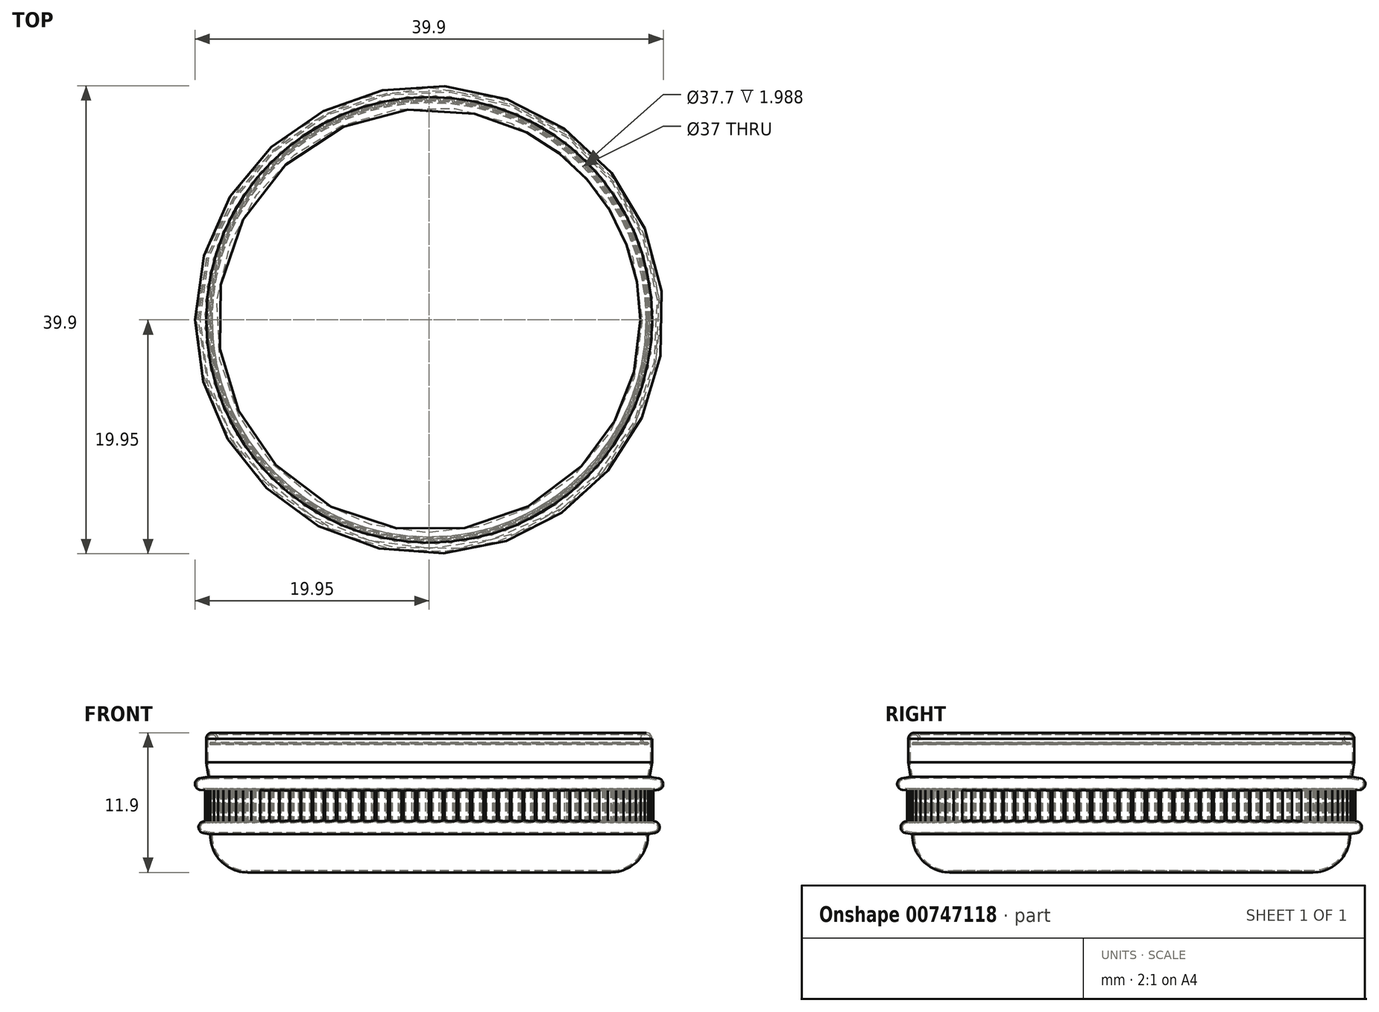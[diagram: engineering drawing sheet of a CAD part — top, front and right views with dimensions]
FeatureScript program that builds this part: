
annotation { "Feature Type Name" : "Feature", "Feature Type Description" : "" }
export const myFeature = defineFeature(function(context is Context, id is Id, definition is map)
    precondition{}
    {
        {
            var Q0;
            Q0=qCreatedBy(makeId("Top.planeOp"),FACE);
            var sketch = newSketch(context, id + "F0", { "sketchPlane" : qUnion([Q0])});
            skCircle(sketch, "E0", {"center": v(0, 0) * mm, "radius": 18.65 * mm});
            skSolve(sketch);
        }
        {
            var Q0;
            Q0 = qSketchRegion(id + "F0", true);
            extrude(context, id + "F1", {"entities" : qUnion([Q0]), "depth" : 11.4 * mm, "offsetDistance" : 25 * mm});
        }
        {
            var Q0;
            Q0=makeQuery(id+"F1.opExtrude","CAP_EDGE",EDGE,{"disambiguationData":[OSD([sQuery(id+"F0.wireOp",EDGE,"E0")])],"isStart":true});
            fillet(context, id + "F2", {"entities" : qUnion([Q0]), "radius" : 3.17 * mm, "tangentPropagation" : true, "allowEdgeOverflow" : false});
        }
        {
            var Q0;
            Q0=makeQuery(id+"F1.opExtrude","CAP_FACE",FACE,{"disambiguationData":[OSD([sQuery(id+"F0.wireOp",EDGE,"E0")])],"isStart":false});
            cPlane(context, id + "F3", {"entities" : qUnion([Q0]), "cplaneType" : CPlaneType.OFFSET, "offset" : 3.25 * mm, "oppositeDirection" : true, "width" : 150 * mm, "height" : 150 * mm});
        }
        {
            var Q0;
            Q0=makeQuery(id+"F1.opExtrude","CAP_FACE",FACE,{"disambiguationData":[OSD([sQuery(id+"F0.wireOp",EDGE,"E0")])],"isStart":false});
            cPlane(context, id + "F4", {"entities" : qUnion([Q0]), "cplaneType" : CPlaneType.OFFSET, "offset" : 8.15 * mm, "oppositeDirection" : true, "width" : 150 * mm, "height" : 150 * mm});
        }
        {
            var Q0;
            Q0=qCreatedBy(makeId("Front.planeOp"),FACE);
            var sketch = newSketch(context, id + "F5", { "sketchPlane" : qUnion([Q0])});
            skLineSegment(sketch, "E1", {"start": v(-18.65, 3.18) * mm, "end": v(-18.65, 8.15) * mm});
            skLineSegment(sketch, "E2", {"start": v(-18.65, 11.4) * mm, "end": v(-18.65, 3.18) * mm});
            skLineSegment(sketch, "E3", {"start": v(-18.65, 6.95) * mm, "end": v(-19.5, 7.03) * mm});
            skLineSegment(sketch, "E4", {"start": v(-18.65, 3.25) * mm, "end": v(-19.24, 3.36) * mm});
            skLineSegment(sketch, "E5", {"start": v(-18.65, 4.45) * mm, "end": v(-19.24, 4.34) * mm});
            skArc(sketch, "E6", {"start": v(-19.53, 8.02) * mm, "mid": v(-19.95, 7.51) * mm, "end": v(-19.5, 7.03) * mm});
            skArc(sketch, "E7", {"start": v(-19.24, 4.34) * mm, "mid": v(-19.65, 3.85) * mm, "end": v(-19.24, 3.36) * mm});
            skLineSegment(sketch, "E8", {"start": v(-19, 11.4) * mm, "end": v(-18.65, 11.4) * mm});
            skLineSegment(sketch, "E9", {"start": v(-19.53, 8.02) * mm, "end": v(-18.8, 8.15) * mm});
            skLineSegment(sketch, "E10", {"start": v(-18.8, 8.15) * mm, "end": v(-19, 9.4) * mm});
            skLineSegment(sketch, "E11", {"start": v(-19, 9.4) * mm, "end": v(-19, 11.4) * mm});
            skSolve(sketch);
        }
        {
            var Q0;
            Q0 = qSketchRegion(id + "F5", true);
            var Q1;
            Q1=makeQuery(id+"F1.opExtrude","CAP_EDGE",EDGE,{"disambiguationData":[OSD([sQuery(id+"F0.wireOp",EDGE,"E0")])],"isStart":false});
            revolve(context, id + "F6", {"operationType" : NewBodyOperationType.ADD, "surfaceOperationType" : NewSurfaceOperationType.NEW, "entities" : qUnion([Q0]), "axis" : qUnion([Q1]), "revolveType" : RevolveType.FULL});
        }
        {
            var Q0;
            Q0=qCreatedBy(id+"F3.planeOp",FACE);
            cPlane(context, id + "F7", {"entities" : qUnion([Q0]), "cplaneType" : CPlaneType.OFFSET, "offset" : 2.45 * mm, "oppositeDirection" : true, "width" : 150 * mm, "height" : 150 * mm});
        }
        {
            var Q0;
            Q0=qCreatedBy(id+"F7.planeOp",FACE);
            var sketch = newSketch(context, id + "F8", { "sketchPlane" : qUnion([Q0])});
            skArc(sketch, "E12", {"start": v(1, 18.57) * mm, "mid": v(0.51, 19.1) * mm, "end": v(0, 18.6) * mm});
            skArc(sketch, "E13", {"start": v(1, 18.57) * mm, "mid": v(0.5, 18.6) * mm, "end": v(0, 18.6) * mm});
            skArc(sketch, "E14.1.0", {"start": v(-0.17, 18.6) * mm, "mid": v(-0.67, 18.59) * mm, "end": v(-1.17, 18.56) * mm});
            skArc(sketch, "E14.1.1", {"start": v(-0.17, 18.6) * mm, "mid": v(-0.69, 19.09) * mm, "end": v(-1.17, 18.56) * mm});
            skArc(sketch, "E14.2.0", {"start": v(-1.34, 18.55) * mm, "mid": v(-1.83, 18.5) * mm, "end": v(-2.33, 18.45) * mm});
            skArc(sketch, "E14.2.1", {"start": v(-1.34, 18.55) * mm, "mid": v(-1.88, 19) * mm, "end": v(-2.33, 18.45) * mm});
            skArc(sketch, "E14.3.0", {"start": v(-2.5, 18.43) * mm, "mid": v(-3, 18.36) * mm, "end": v(-3.49, 18.27) * mm});
            skArc(sketch, "E14.3.1", {"start": v(-2.5, 18.43) * mm, "mid": v(-3.07, 18.85) * mm, "end": v(-3.49, 18.27) * mm});
            skArc(sketch, "E14.4.0", {"start": v(-3.65, 18.24) * mm, "mid": v(-4.14, 18.13) * mm, "end": v(-4.63, 18.02) * mm});
            skArc(sketch, "E14.4.1", {"start": v(-3.65, 18.24) * mm, "mid": v(-4.25, 18.62) * mm, "end": v(-4.63, 18.02) * mm});
            skArc(sketch, "E14.5.0", {"start": v(-4.79, 17.97) * mm, "mid": v(-5.27, 17.84) * mm, "end": v(-5.75, 17.69) * mm});
            skArc(sketch, "E14.5.1", {"start": v(-4.79, 17.97) * mm, "mid": v(-5.41, 18.32) * mm, "end": v(-5.75, 17.69) * mm});
            skArc(sketch, "E14.6.0", {"start": v(-5.9, 17.64) * mm, "mid": v(-6.38, 17.47) * mm, "end": v(-6.85, 17.3) * mm});
            skArc(sketch, "E14.6.1", {"start": v(-5.9, 17.64) * mm, "mid": v(-6.55, 17.94) * mm, "end": v(-6.85, 17.3) * mm});
            skArc(sketch, "E14.7.0", {"start": v(-7, 17.23) * mm, "mid": v(-7.46, 17.04) * mm, "end": v(-7.92, 16.83) * mm});
            skArc(sketch, "E14.7.1", {"start": v(-7, 17.23) * mm, "mid": v(-7.66, 17.5) * mm, "end": v(-7.92, 16.83) * mm});
            skArc(sketch, "E14.8.0", {"start": v(-8.07, 16.76) * mm, "mid": v(-8.52, 16.53) * mm, "end": v(-8.96, 16.3) * mm});
            skArc(sketch, "E14.8.1", {"start": v(-8.07, 16.76) * mm, "mid": v(-8.75, 16.98) * mm, "end": v(-8.96, 16.3) * mm});
            skArc(sketch, "E14.9.0", {"start": v(-9.1, 16.22) * mm, "mid": v(-9.54, 15.97) * mm, "end": v(-9.97, 15.7) * mm});
            skArc(sketch, "E14.9.1", {"start": v(-9.1, 16.22) * mm, "mid": v(-9.8, 16.4) * mm, "end": v(-9.97, 15.7) * mm});
            skArc(sketch, "E14.10.0", {"start": v(-10.1, 15.61) * mm, "mid": v(-10.52, 15.34) * mm, "end": v(-10.93, 15.05) * mm});
            skArc(sketch, "E14.10.1", {"start": v(-10.1, 15.61) * mm, "mid": v(-10.8, 15.75) * mm, "end": v(-10.93, 15.05) * mm});
            skArc(sketch, "E14.11.0", {"start": v(-11.07, 14.95) * mm, "mid": v(-11.47, 14.65) * mm, "end": v(-11.86, 14.33) * mm});
            skArc(sketch, "E14.11.1", {"start": v(-11.07, 14.95) * mm, "mid": v(-11.77, 15.04) * mm, "end": v(-11.86, 14.33) * mm});
            skArc(sketch, "E14.12.0", {"start": v(-11.99, 14.22) * mm, "mid": v(-12.36, 13.9) * mm, "end": v(-12.73, 13.56) * mm});
            skArc(sketch, "E14.12.1", {"start": v(-11.99, 14.22) * mm, "mid": v(-12.7, 14.27) * mm, "end": v(-12.73, 13.56) * mm});
            skArc(sketch, "E14.13.0", {"start": v(-12.85, 13.44) * mm, "mid": v(-13.21, 13.1) * mm, "end": v(-13.56, 12.73) * mm});
            skArc(sketch, "E14.13.1", {"start": v(-12.85, 13.44) * mm, "mid": v(-13.57, 13.44) * mm, "end": v(-13.56, 12.73) * mm});
            skArc(sketch, "E14.14.0", {"start": v(-13.67, 12.6) * mm, "mid": v(-14, 12.24) * mm, "end": v(-14.33, 11.86) * mm});
            skArc(sketch, "E14.14.1", {"start": v(-13.67, 12.6) * mm, "mid": v(-14.38, 12.57) * mm, "end": v(-14.33, 11.86) * mm});
            skArc(sketch, "E14.15.0", {"start": v(-14.44, 11.73) * mm, "mid": v(-14.75, 11.33) * mm, "end": v(-15.05, 10.93) * mm});
            skArc(sketch, "E14.15.1", {"start": v(-14.44, 11.73) * mm, "mid": v(-15.14, 11.64) * mm, "end": v(-15.05, 10.93) * mm});
            skArc(sketch, "E14.16.0", {"start": v(-15.15, 10.8) * mm, "mid": v(-15.43, 10.38) * mm, "end": v(-15.7, 9.97) * mm});
            skArc(sketch, "E14.16.1", {"start": v(-15.15, 10.8) * mm, "mid": v(-15.85, 10.66) * mm, "end": v(-15.7, 9.97) * mm});
            skArc(sketch, "E14.17.0", {"start": v(-15.8, 9.82) * mm, "mid": v(-16.05, 9.4) * mm, "end": v(-16.3, 8.96) * mm});
            skArc(sketch, "E14.17.1", {"start": v(-15.8, 9.82) * mm, "mid": v(-16.48, 9.65) * mm, "end": v(-16.3, 8.96) * mm});
            skArc(sketch, "E14.18.0", {"start": v(-16.38, 8.81) * mm, "mid": v(-16.61, 8.37) * mm, "end": v(-16.83, 7.92) * mm});
            skArc(sketch, "E14.18.1", {"start": v(-16.38, 8.81) * mm, "mid": v(-17.06, 8.6) * mm, "end": v(-16.83, 7.92) * mm});
            skArc(sketch, "E14.19.0", {"start": v(-16.9, 7.77) * mm, "mid": v(-17.1, 7.3) * mm, "end": v(-17.3, 6.85) * mm});
            skArc(sketch, "E14.19.1", {"start": v(-16.9, 7.77) * mm, "mid": v(-17.56, 7.5) * mm, "end": v(-17.3, 6.85) * mm});
            skArc(sketch, "E14.20.0", {"start": v(-17.36, 6.7) * mm, "mid": v(-17.53, 6.22) * mm, "end": v(-17.69, 5.75) * mm});
            skArc(sketch, "E14.20.1", {"start": v(-17.36, 6.7) * mm, "mid": v(-18, 6.39) * mm, "end": v(-17.69, 5.75) * mm});
            skArc(sketch, "E14.21.0", {"start": v(-17.74, 5.59) * mm, "mid": v(-17.88, 5.1) * mm, "end": v(-18.02, 4.63) * mm});
            skArc(sketch, "E14.21.1", {"start": v(-17.74, 5.59) * mm, "mid": v(-18.37, 5.25) * mm, "end": v(-18.02, 4.63) * mm});
            skArc(sketch, "E14.22.0", {"start": v(-18.06, 4.46) * mm, "mid": v(-18.17, 3.98) * mm, "end": v(-18.27, 3.49) * mm});
            skArc(sketch, "E14.22.1", {"start": v(-18.06, 4.46) * mm, "mid": v(-18.66, 4.08) * mm, "end": v(-18.27, 3.49) * mm});
            skArc(sketch, "E14.23.0", {"start": v(-18.3, 3.32) * mm, "mid": v(-18.38, 2.83) * mm, "end": v(-18.45, 2.33) * mm});
            skArc(sketch, "E14.23.1", {"start": v(-18.3, 3.32) * mm, "mid": v(-18.88, 2.9) * mm, "end": v(-18.45, 2.33) * mm});
            skArc(sketch, "E14.24.0", {"start": v(-18.47, 2.16) * mm, "mid": v(-18.53, 1.67) * mm, "end": v(-18.56, 1.17) * mm});
            skArc(sketch, "E14.24.1", {"start": v(-18.47, 2.16) * mm, "mid": v(-19.02, 1.71) * mm, "end": v(-18.56, 1.17) * mm});
            skArc(sketch, "E14.25.0", {"start": v(-18.57, 1) * mm, "mid": v(-18.6, 0.5) * mm, "end": v(-18.6, 0) * mm});
            skArc(sketch, "E14.25.1", {"start": v(-18.57, 1) * mm, "mid": v(-19.1, 0.51) * mm, "end": v(-18.6, 0) * mm});
            skArc(sketch, "E14.26.0", {"start": v(-18.6, -0.17) * mm, "mid": v(-18.59, -0.67) * mm, "end": v(-18.56, -1.17) * mm});
            skArc(sketch, "E14.26.1", {"start": v(-18.6, -0.17) * mm, "mid": v(-19.09, -0.69) * mm, "end": v(-18.56, -1.17) * mm});
            skArc(sketch, "E14.27.0", {"start": v(-18.55, -1.34) * mm, "mid": v(-18.5, -1.83) * mm, "end": v(-18.45, -2.33) * mm});
            skArc(sketch, "E14.27.1", {"start": v(-18.55, -1.34) * mm, "mid": v(-19, -1.88) * mm, "end": v(-18.45, -2.33) * mm});
            skArc(sketch, "E14.28.0", {"start": v(-18.43, -2.5) * mm, "mid": v(-18.36, -3) * mm, "end": v(-18.27, -3.49) * mm});
            skArc(sketch, "E14.28.1", {"start": v(-18.43, -2.5) * mm, "mid": v(-18.85, -3.07) * mm, "end": v(-18.27, -3.49) * mm});
            skArc(sketch, "E14.29.0", {"start": v(-18.24, -3.65) * mm, "mid": v(-18.13, -4.14) * mm, "end": v(-18.02, -4.63) * mm});
            skArc(sketch, "E14.29.1", {"start": v(-18.24, -3.65) * mm, "mid": v(-18.62, -4.25) * mm, "end": v(-18.02, -4.63) * mm});
            skArc(sketch, "E14.30.0", {"start": v(-17.97, -4.79) * mm, "mid": v(-17.84, -5.27) * mm, "end": v(-17.69, -5.75) * mm});
            skArc(sketch, "E14.30.1", {"start": v(-17.97, -4.79) * mm, "mid": v(-18.32, -5.41) * mm, "end": v(-17.69, -5.75) * mm});
            skArc(sketch, "E14.31.0", {"start": v(-17.64, -5.9) * mm, "mid": v(-17.47, -6.38) * mm, "end": v(-17.3, -6.85) * mm});
            skArc(sketch, "E14.31.1", {"start": v(-17.64, -5.9) * mm, "mid": v(-17.94, -6.55) * mm, "end": v(-17.3, -6.85) * mm});
            skArc(sketch, "E14.32.0", {"start": v(-17.23, -7) * mm, "mid": v(-17.04, -7.46) * mm, "end": v(-16.83, -7.92) * mm});
            skArc(sketch, "E14.32.1", {"start": v(-17.23, -7) * mm, "mid": v(-17.5, -7.66) * mm, "end": v(-16.83, -7.92) * mm});
            skArc(sketch, "E14.33.0", {"start": v(-16.76, -8.07) * mm, "mid": v(-16.53, -8.52) * mm, "end": v(-16.3, -8.96) * mm});
            skArc(sketch, "E14.33.1", {"start": v(-16.76, -8.07) * mm, "mid": v(-16.98, -8.75) * mm, "end": v(-16.3, -8.96) * mm});
            skArc(sketch, "E14.34.0", {"start": v(-16.22, -9.1) * mm, "mid": v(-15.97, -9.54) * mm, "end": v(-15.7, -9.97) * mm});
            skArc(sketch, "E14.34.1", {"start": v(-16.22, -9.1) * mm, "mid": v(-16.4, -9.8) * mm, "end": v(-15.7, -9.97) * mm});
            skArc(sketch, "E14.35.0", {"start": v(-15.61, -10.1) * mm, "mid": v(-15.34, -10.52) * mm, "end": v(-15.05, -10.93) * mm});
            skArc(sketch, "E14.35.1", {"start": v(-15.61, -10.1) * mm, "mid": v(-15.75, -10.8) * mm, "end": v(-15.05, -10.93) * mm});
            skArc(sketch, "E14.36.0", {"start": v(-14.95, -11.07) * mm, "mid": v(-14.65, -11.47) * mm, "end": v(-14.33, -11.86) * mm});
            skArc(sketch, "E14.36.1", {"start": v(-14.95, -11.07) * mm, "mid": v(-15.04, -11.77) * mm, "end": v(-14.33, -11.86) * mm});
            skArc(sketch, "E14.37.0", {"start": v(-14.22, -11.99) * mm, "mid": v(-13.9, -12.36) * mm, "end": v(-13.56, -12.73) * mm});
            skArc(sketch, "E14.37.1", {"start": v(-14.22, -11.99) * mm, "mid": v(-14.27, -12.7) * mm, "end": v(-13.56, -12.73) * mm});
            skArc(sketch, "E14.38.0", {"start": v(-13.44, -12.85) * mm, "mid": v(-13.1, -13.21) * mm, "end": v(-12.73, -13.56) * mm});
            skArc(sketch, "E14.38.1", {"start": v(-13.44, -12.85) * mm, "mid": v(-13.44, -13.57) * mm, "end": v(-12.73, -13.56) * mm});
            skArc(sketch, "E14.39.0", {"start": v(-12.6, -13.67) * mm, "mid": v(-12.24, -14) * mm, "end": v(-11.86, -14.33) * mm});
            skArc(sketch, "E14.39.1", {"start": v(-12.6, -13.67) * mm, "mid": v(-12.57, -14.38) * mm, "end": v(-11.86, -14.33) * mm});
            skArc(sketch, "E14.40.0", {"start": v(-11.73, -14.44) * mm, "mid": v(-11.33, -14.75) * mm, "end": v(-10.93, -15.05) * mm});
            skArc(sketch, "E14.40.1", {"start": v(-11.73, -14.44) * mm, "mid": v(-11.64, -15.14) * mm, "end": v(-10.93, -15.05) * mm});
            skArc(sketch, "E14.41.0", {"start": v(-10.8, -15.15) * mm, "mid": v(-10.38, -15.43) * mm, "end": v(-9.97, -15.7) * mm});
            skArc(sketch, "E14.41.1", {"start": v(-10.8, -15.15) * mm, "mid": v(-10.66, -15.85) * mm, "end": v(-9.97, -15.7) * mm});
            skArc(sketch, "E14.42.0", {"start": v(-9.82, -15.8) * mm, "mid": v(-9.4, -16.05) * mm, "end": v(-8.96, -16.3) * mm});
            skArc(sketch, "E14.42.1", {"start": v(-9.82, -15.8) * mm, "mid": v(-9.65, -16.48) * mm, "end": v(-8.96, -16.3) * mm});
            skArc(sketch, "E14.43.0", {"start": v(-8.81, -16.38) * mm, "mid": v(-8.37, -16.61) * mm, "end": v(-7.92, -16.83) * mm});
            skArc(sketch, "E14.43.1", {"start": v(-8.81, -16.38) * mm, "mid": v(-8.6, -17.06) * mm, "end": v(-7.92, -16.83) * mm});
            skArc(sketch, "E14.44.0", {"start": v(-7.77, -16.9) * mm, "mid": v(-7.3, -17.1) * mm, "end": v(-6.85, -17.3) * mm});
            skArc(sketch, "E14.44.1", {"start": v(-7.77, -16.9) * mm, "mid": v(-7.5, -17.56) * mm, "end": v(-6.85, -17.3) * mm});
            skArc(sketch, "E14.45.0", {"start": v(-6.7, -17.36) * mm, "mid": v(-6.22, -17.53) * mm, "end": v(-5.75, -17.69) * mm});
            skArc(sketch, "E14.45.1", {"start": v(-6.7, -17.36) * mm, "mid": v(-6.39, -18) * mm, "end": v(-5.75, -17.69) * mm});
            skArc(sketch, "E14.46.0", {"start": v(-5.59, -17.74) * mm, "mid": v(-5.1, -17.88) * mm, "end": v(-4.63, -18.02) * mm});
            skArc(sketch, "E14.46.1", {"start": v(-5.59, -17.74) * mm, "mid": v(-5.25, -18.37) * mm, "end": v(-4.63, -18.02) * mm});
            skArc(sketch, "E14.47.0", {"start": v(-4.46, -18.06) * mm, "mid": v(-3.98, -18.17) * mm, "end": v(-3.49, -18.27) * mm});
            skArc(sketch, "E14.47.1", {"start": v(-4.46, -18.06) * mm, "mid": v(-4.08, -18.66) * mm, "end": v(-3.49, -18.27) * mm});
            skArc(sketch, "E14.48.0", {"start": v(-3.32, -18.3) * mm, "mid": v(-2.83, -18.38) * mm, "end": v(-2.33, -18.45) * mm});
            skArc(sketch, "E14.48.1", {"start": v(-3.32, -18.3) * mm, "mid": v(-2.9, -18.88) * mm, "end": v(-2.33, -18.45) * mm});
            skArc(sketch, "E14.49.0", {"start": v(-2.16, -18.47) * mm, "mid": v(-1.67, -18.53) * mm, "end": v(-1.17, -18.56) * mm});
            skArc(sketch, "E14.49.1", {"start": v(-2.16, -18.47) * mm, "mid": v(-1.71, -19.02) * mm, "end": v(-1.17, -18.56) * mm});
            skArc(sketch, "E14.50.0", {"start": v(-1, -18.57) * mm, "mid": v(-0.5, -18.6) * mm, "end": v(0, -18.6) * mm});
            skArc(sketch, "E14.50.1", {"start": v(-1, -18.57) * mm, "mid": v(-0.51, -19.1) * mm, "end": v(0, -18.6) * mm});
            skArc(sketch, "E14.51.0", {"start": v(0.17, -18.6) * mm, "mid": v(0.67, -18.59) * mm, "end": v(1.17, -18.56) * mm});
            skArc(sketch, "E14.51.1", {"start": v(0.17, -18.6) * mm, "mid": v(0.69, -19.09) * mm, "end": v(1.17, -18.56) * mm});
            skArc(sketch, "E14.52.0", {"start": v(1.34, -18.55) * mm, "mid": v(1.83, -18.5) * mm, "end": v(2.33, -18.45) * mm});
            skArc(sketch, "E14.52.1", {"start": v(1.34, -18.55) * mm, "mid": v(1.88, -19) * mm, "end": v(2.33, -18.45) * mm});
            skArc(sketch, "E14.53.0", {"start": v(2.5, -18.43) * mm, "mid": v(3, -18.36) * mm, "end": v(3.49, -18.27) * mm});
            skArc(sketch, "E14.53.1", {"start": v(2.5, -18.43) * mm, "mid": v(3.07, -18.85) * mm, "end": v(3.49, -18.27) * mm});
            skArc(sketch, "E14.54.0", {"start": v(3.65, -18.24) * mm, "mid": v(4.14, -18.13) * mm, "end": v(4.63, -18.02) * mm});
            skArc(sketch, "E14.54.1", {"start": v(3.65, -18.24) * mm, "mid": v(4.25, -18.62) * mm, "end": v(4.63, -18.02) * mm});
            skArc(sketch, "E14.55.0", {"start": v(4.79, -17.97) * mm, "mid": v(5.27, -17.84) * mm, "end": v(5.75, -17.69) * mm});
            skArc(sketch, "E14.55.1", {"start": v(4.79, -17.97) * mm, "mid": v(5.41, -18.32) * mm, "end": v(5.75, -17.69) * mm});
            skArc(sketch, "E14.56.0", {"start": v(5.9, -17.64) * mm, "mid": v(6.38, -17.47) * mm, "end": v(6.85, -17.3) * mm});
            skArc(sketch, "E14.56.1", {"start": v(5.9, -17.64) * mm, "mid": v(6.55, -17.94) * mm, "end": v(6.85, -17.3) * mm});
            skArc(sketch, "E14.57.0", {"start": v(7, -17.23) * mm, "mid": v(7.46, -17.04) * mm, "end": v(7.92, -16.83) * mm});
            skArc(sketch, "E14.57.1", {"start": v(7, -17.23) * mm, "mid": v(7.66, -17.5) * mm, "end": v(7.92, -16.83) * mm});
            skArc(sketch, "E14.58.0", {"start": v(8.07, -16.76) * mm, "mid": v(8.52, -16.53) * mm, "end": v(8.96, -16.3) * mm});
            skArc(sketch, "E14.58.1", {"start": v(8.07, -16.76) * mm, "mid": v(8.75, -16.98) * mm, "end": v(8.96, -16.3) * mm});
            skArc(sketch, "E14.59.0", {"start": v(9.1, -16.22) * mm, "mid": v(9.54, -15.97) * mm, "end": v(9.97, -15.7) * mm});
            skArc(sketch, "E14.59.1", {"start": v(9.1, -16.22) * mm, "mid": v(9.8, -16.4) * mm, "end": v(9.97, -15.7) * mm});
            skArc(sketch, "E14.60.0", {"start": v(10.1, -15.61) * mm, "mid": v(10.52, -15.34) * mm, "end": v(10.93, -15.05) * mm});
            skArc(sketch, "E14.60.1", {"start": v(10.1, -15.61) * mm, "mid": v(10.8, -15.75) * mm, "end": v(10.93, -15.05) * mm});
            skArc(sketch, "E14.61.0", {"start": v(11.07, -14.95) * mm, "mid": v(11.47, -14.65) * mm, "end": v(11.86, -14.33) * mm});
            skArc(sketch, "E14.61.1", {"start": v(11.07, -14.95) * mm, "mid": v(11.77, -15.04) * mm, "end": v(11.86, -14.33) * mm});
            skArc(sketch, "E14.62.0", {"start": v(11.99, -14.22) * mm, "mid": v(12.36, -13.9) * mm, "end": v(12.73, -13.56) * mm});
            skArc(sketch, "E14.62.1", {"start": v(11.99, -14.22) * mm, "mid": v(12.7, -14.27) * mm, "end": v(12.73, -13.56) * mm});
            skArc(sketch, "E14.63.0", {"start": v(12.85, -13.44) * mm, "mid": v(13.21, -13.1) * mm, "end": v(13.56, -12.73) * mm});
            skArc(sketch, "E14.63.1", {"start": v(12.85, -13.44) * mm, "mid": v(13.57, -13.44) * mm, "end": v(13.56, -12.73) * mm});
            skArc(sketch, "E14.64.0", {"start": v(13.67, -12.6) * mm, "mid": v(14, -12.24) * mm, "end": v(14.33, -11.86) * mm});
            skArc(sketch, "E14.64.1", {"start": v(13.67, -12.6) * mm, "mid": v(14.38, -12.57) * mm, "end": v(14.33, -11.86) * mm});
            skArc(sketch, "E14.65.0", {"start": v(14.44, -11.73) * mm, "mid": v(14.75, -11.33) * mm, "end": v(15.05, -10.93) * mm});
            skArc(sketch, "E14.65.1", {"start": v(14.44, -11.73) * mm, "mid": v(15.14, -11.64) * mm, "end": v(15.05, -10.93) * mm});
            skArc(sketch, "E14.66.0", {"start": v(15.15, -10.8) * mm, "mid": v(15.43, -10.38) * mm, "end": v(15.7, -9.97) * mm});
            skArc(sketch, "E14.66.1", {"start": v(15.15, -10.8) * mm, "mid": v(15.85, -10.66) * mm, "end": v(15.7, -9.97) * mm});
            skArc(sketch, "E14.67.0", {"start": v(15.8, -9.82) * mm, "mid": v(16.05, -9.4) * mm, "end": v(16.3, -8.96) * mm});
            skArc(sketch, "E14.67.1", {"start": v(15.8, -9.82) * mm, "mid": v(16.48, -9.65) * mm, "end": v(16.3, -8.96) * mm});
            skArc(sketch, "E14.68.0", {"start": v(16.38, -8.81) * mm, "mid": v(16.61, -8.37) * mm, "end": v(16.83, -7.92) * mm});
            skArc(sketch, "E14.68.1", {"start": v(16.38, -8.81) * mm, "mid": v(17.06, -8.6) * mm, "end": v(16.83, -7.92) * mm});
            skArc(sketch, "E14.69.0", {"start": v(16.9, -7.77) * mm, "mid": v(17.1, -7.3) * mm, "end": v(17.3, -6.85) * mm});
            skArc(sketch, "E14.69.1", {"start": v(16.9, -7.77) * mm, "mid": v(17.56, -7.5) * mm, "end": v(17.3, -6.85) * mm});
            skArc(sketch, "E14.70.0", {"start": v(17.36, -6.7) * mm, "mid": v(17.53, -6.22) * mm, "end": v(17.69, -5.75) * mm});
            skArc(sketch, "E14.70.1", {"start": v(17.36, -6.7) * mm, "mid": v(18, -6.39) * mm, "end": v(17.69, -5.75) * mm});
            skArc(sketch, "E14.71.0", {"start": v(17.74, -5.59) * mm, "mid": v(17.88, -5.1) * mm, "end": v(18.02, -4.63) * mm});
            skArc(sketch, "E14.71.1", {"start": v(17.74, -5.59) * mm, "mid": v(18.37, -5.25) * mm, "end": v(18.02, -4.63) * mm});
            skArc(sketch, "E14.72.0", {"start": v(18.06, -4.46) * mm, "mid": v(18.17, -3.98) * mm, "end": v(18.27, -3.49) * mm});
            skArc(sketch, "E14.72.1", {"start": v(18.06, -4.46) * mm, "mid": v(18.66, -4.08) * mm, "end": v(18.27, -3.49) * mm});
            skArc(sketch, "E14.73.0", {"start": v(18.3, -3.32) * mm, "mid": v(18.38, -2.83) * mm, "end": v(18.45, -2.33) * mm});
            skArc(sketch, "E14.73.1", {"start": v(18.3, -3.32) * mm, "mid": v(18.88, -2.9) * mm, "end": v(18.45, -2.33) * mm});
            skArc(sketch, "E14.74.0", {"start": v(18.47, -2.16) * mm, "mid": v(18.53, -1.67) * mm, "end": v(18.56, -1.17) * mm});
            skArc(sketch, "E14.74.1", {"start": v(18.47, -2.16) * mm, "mid": v(19.02, -1.71) * mm, "end": v(18.56, -1.17) * mm});
            skArc(sketch, "E14.75.0", {"start": v(18.57, -1) * mm, "mid": v(18.6, -0.5) * mm, "end": v(18.6, 0) * mm});
            skArc(sketch, "E14.75.1", {"start": v(18.57, -1) * mm, "mid": v(19.1, -0.51) * mm, "end": v(18.6, 0) * mm});
            skArc(sketch, "E14.76.0", {"start": v(18.6, 0.17) * mm, "mid": v(18.59, 0.67) * mm, "end": v(18.56, 1.17) * mm});
            skArc(sketch, "E14.76.1", {"start": v(18.6, 0.17) * mm, "mid": v(19.09, 0.69) * mm, "end": v(18.56, 1.17) * mm});
            skArc(sketch, "E14.77.0", {"start": v(18.55, 1.34) * mm, "mid": v(18.5, 1.83) * mm, "end": v(18.45, 2.33) * mm});
            skArc(sketch, "E14.77.1", {"start": v(18.55, 1.34) * mm, "mid": v(19, 1.88) * mm, "end": v(18.45, 2.33) * mm});
            skArc(sketch, "E14.78.0", {"start": v(18.43, 2.5) * mm, "mid": v(18.36, 3) * mm, "end": v(18.27, 3.49) * mm});
            skArc(sketch, "E14.78.1", {"start": v(18.43, 2.5) * mm, "mid": v(18.85, 3.07) * mm, "end": v(18.27, 3.49) * mm});
            skArc(sketch, "E14.79.0", {"start": v(18.24, 3.65) * mm, "mid": v(18.13, 4.14) * mm, "end": v(18.02, 4.63) * mm});
            skArc(sketch, "E14.79.1", {"start": v(18.24, 3.65) * mm, "mid": v(18.62, 4.25) * mm, "end": v(18.02, 4.63) * mm});
            skArc(sketch, "E14.80.0", {"start": v(17.97, 4.79) * mm, "mid": v(17.84, 5.27) * mm, "end": v(17.69, 5.75) * mm});
            skArc(sketch, "E14.80.1", {"start": v(17.97, 4.79) * mm, "mid": v(18.32, 5.41) * mm, "end": v(17.69, 5.75) * mm});
            skArc(sketch, "E14.81.0", {"start": v(17.64, 5.9) * mm, "mid": v(17.47, 6.38) * mm, "end": v(17.3, 6.85) * mm});
            skArc(sketch, "E14.81.1", {"start": v(17.64, 5.9) * mm, "mid": v(17.94, 6.55) * mm, "end": v(17.3, 6.85) * mm});
            skArc(sketch, "E14.82.0", {"start": v(17.23, 7) * mm, "mid": v(17.04, 7.46) * mm, "end": v(16.83, 7.92) * mm});
            skArc(sketch, "E14.82.1", {"start": v(17.23, 7) * mm, "mid": v(17.5, 7.66) * mm, "end": v(16.83, 7.92) * mm});
            skArc(sketch, "E14.83.0", {"start": v(16.76, 8.07) * mm, "mid": v(16.53, 8.52) * mm, "end": v(16.3, 8.96) * mm});
            skArc(sketch, "E14.83.1", {"start": v(16.76, 8.07) * mm, "mid": v(16.98, 8.75) * mm, "end": v(16.3, 8.96) * mm});
            skArc(sketch, "E14.84.0", {"start": v(16.22, 9.1) * mm, "mid": v(15.97, 9.54) * mm, "end": v(15.7, 9.97) * mm});
            skArc(sketch, "E14.84.1", {"start": v(16.22, 9.1) * mm, "mid": v(16.4, 9.8) * mm, "end": v(15.7, 9.97) * mm});
            skArc(sketch, "E15.3.85.0", {"start": v(15.61, 10.1) * mm, "mid": v(15.34, 10.52) * mm, "end": v(15.05, 10.93) * mm});
            skArc(sketch, "E15.4.85.0", {"start": v(15.61, 10.1) * mm, "mid": v(15.75, 10.8) * mm, "end": v(15.05, 10.93) * mm});
            skArc(sketch, "E15.3.86.0", {"start": v(14.95, 11.07) * mm, "mid": v(14.65, 11.47) * mm, "end": v(14.33, 11.86) * mm});
            skArc(sketch, "E15.4.86.0", {"start": v(14.95, 11.07) * mm, "mid": v(15.04, 11.77) * mm, "end": v(14.33, 11.86) * mm});
            skArc(sketch, "E15.3.87.0", {"start": v(14.22, 11.99) * mm, "mid": v(13.9, 12.36) * mm, "end": v(13.56, 12.73) * mm});
            skArc(sketch, "E15.4.87.0", {"start": v(14.22, 11.99) * mm, "mid": v(14.27, 12.7) * mm, "end": v(13.56, 12.73) * mm});
            skArc(sketch, "E15.3.88.0", {"start": v(13.44, 12.85) * mm, "mid": v(13.1, 13.21) * mm, "end": v(12.73, 13.56) * mm});
            skArc(sketch, "E15.4.88.0", {"start": v(13.44, 12.85) * mm, "mid": v(13.44, 13.57) * mm, "end": v(12.73, 13.56) * mm});
            skArc(sketch, "E15.3.89.0", {"start": v(12.6, 13.67) * mm, "mid": v(12.24, 14) * mm, "end": v(11.86, 14.33) * mm});
            skArc(sketch, "E15.4.89.0", {"start": v(12.6, 13.67) * mm, "mid": v(12.57, 14.38) * mm, "end": v(11.86, 14.33) * mm});
            skArc(sketch, "E15.3.90.0", {"start": v(11.73, 14.44) * mm, "mid": v(11.33, 14.75) * mm, "end": v(10.93, 15.05) * mm});
            skArc(sketch, "E15.4.90.0", {"start": v(11.73, 14.44) * mm, "mid": v(11.64, 15.14) * mm, "end": v(10.93, 15.05) * mm});
            skArc(sketch, "E15.3.91.0", {"start": v(10.8, 15.15) * mm, "mid": v(10.38, 15.43) * mm, "end": v(9.97, 15.7) * mm});
            skArc(sketch, "E15.4.91.0", {"start": v(10.8, 15.15) * mm, "mid": v(10.66, 15.85) * mm, "end": v(9.97, 15.7) * mm});
            skArc(sketch, "E15.3.92.0", {"start": v(9.82, 15.8) * mm, "mid": v(9.4, 16.05) * mm, "end": v(8.96, 16.3) * mm});
            skArc(sketch, "E15.4.92.0", {"start": v(9.82, 15.8) * mm, "mid": v(9.65, 16.48) * mm, "end": v(8.96, 16.3) * mm});
            skArc(sketch, "E15.3.93.0", {"start": v(8.81, 16.38) * mm, "mid": v(8.37, 16.61) * mm, "end": v(7.92, 16.83) * mm});
            skArc(sketch, "E15.4.93.0", {"start": v(8.81, 16.38) * mm, "mid": v(8.6, 17.06) * mm, "end": v(7.92, 16.83) * mm});
            skArc(sketch, "E15.3.94.0", {"start": v(7.77, 16.9) * mm, "mid": v(7.3, 17.1) * mm, "end": v(6.85, 17.3) * mm});
            skArc(sketch, "E15.4.94.0", {"start": v(7.77, 16.9) * mm, "mid": v(7.5, 17.56) * mm, "end": v(6.85, 17.3) * mm});
            skArc(sketch, "E15.3.95.0", {"start": v(6.7, 17.36) * mm, "mid": v(6.22, 17.53) * mm, "end": v(5.75, 17.69) * mm});
            skArc(sketch, "E15.4.95.0", {"start": v(6.7, 17.36) * mm, "mid": v(6.39, 18) * mm, "end": v(5.75, 17.69) * mm});
            skArc(sketch, "E15.3.96.0", {"start": v(5.59, 17.74) * mm, "mid": v(5.1, 17.88) * mm, "end": v(4.63, 18.02) * mm});
            skArc(sketch, "E15.4.96.0", {"start": v(5.59, 17.74) * mm, "mid": v(5.25, 18.37) * mm, "end": v(4.63, 18.02) * mm});
            skArc(sketch, "E15.3.97.0", {"start": v(4.46, 18.06) * mm, "mid": v(3.98, 18.17) * mm, "end": v(3.49, 18.27) * mm});
            skArc(sketch, "E15.4.97.0", {"start": v(4.46, 18.06) * mm, "mid": v(4.08, 18.66) * mm, "end": v(3.49, 18.27) * mm});
            skArc(sketch, "E15.3.98.0", {"start": v(3.32, 18.3) * mm, "mid": v(2.83, 18.38) * mm, "end": v(2.33, 18.45) * mm});
            skArc(sketch, "E15.4.98.0", {"start": v(3.32, 18.3) * mm, "mid": v(2.9, 18.88) * mm, "end": v(2.33, 18.45) * mm});
            skArc(sketch, "E15.3.99.0", {"start": v(2.16, 18.47) * mm, "mid": v(1.67, 18.53) * mm, "end": v(1.17, 18.56) * mm});
            skArc(sketch, "E15.4.99.0", {"start": v(2.16, 18.47) * mm, "mid": v(1.71, 19.02) * mm, "end": v(1.17, 18.56) * mm});
            skSolve(sketch);
        }
        {
            var Q0;
            Q0 = qSketchRegion(id + "F8", true);
            var Q1;
            Q1=makeQuery(id+"F6.opRevolve","SWEPT_FACE",FACE,{"disambiguationData":[OSD([sQuery(id+"F5.wireOp",EDGE,"E6")])]});
            extrude(context, id + "F9", {"entities" : qUnion([Q0]), "operationType" : NewBodyOperationType.ADD, "depth" : 2.25 * mm, "endBoundEntityFace" : qUnion([Q1]), "offsetDistance" : 25 * mm});
        }
        {
            var Q0;
            Q0 = qSketchRegion(id + "F8", true);
            extrude(context, id + "F10", {"entities" : qUnion([Q0]), "operationType" : NewBodyOperationType.ADD, "oppositeDirection" : true, "depth" : 2.3 * mm, "offsetDistance" : 25 * mm});
        }
        {
            var Q0;
            Q0=makeQuery(id+"F6.boolean.opBoolean","MERGE",FACE,{"derivedFrom":[makeQuery(id+"F1.opExtrude","CAP_FACE",FACE,{"disambiguationData":[OSD([sQuery(id+"F0.wireOp",EDGE,"E0")])],"isStart":false}),makeQuery(id+"F6.opRevolve","SWEPT_FACE",FACE,{"disambiguationData":[OSD([sQuery(id+"F5.wireOp",EDGE,"E8")])]})]});
            shell(context, id + "F11", {"entities" : qUnion([Q0]), "thickness" : .15 * mm});
        }
        {
            var Q0;
            Q0=qCreatedBy(makeId("Front.planeOp"),FACE);
            var sketch = newSketch(context, id + "F12", { "sketchPlane" : qUnion([Q0])});
            skArc(sketch, "E16", {"start": v(-18.7, 10.94) * mm, "mid": v(-18.08, 11.67) * mm, "end": v(-19, 11.4) * mm});
            skArc(sketch, "E17", {"start": v(-18.64, 11.08) * mm, "mid": v(-18.2, 11.6) * mm, "end": v(-18.85, 11.4) * mm});
            skLineSegment(sketch, "E18", {"start": v(-18.7, 10.94) * mm, "end": v(-18.64, 11.08) * mm});
            skLineSegment(sketch, "E19", {"start": v(-19, 11.4) * mm, "end": v(-18.85, 11.4) * mm});
            skSolve(sketch);
        }
        {
            var Q0;
            Q0 = qSketchRegion(id + "F12", true);
            var Q1;
            Q1=makeQuery(id+"F6.opRevolve","SWEPT_EDGE",EDGE,{"disambiguationData":[OSD([sQuery(id+"F5.wireOp",EDGE,"E8"),sQuery(id+"F5.wireOp",EDGE,"E11")])]});
            revolve(context, id + "F13", {"surfaceOperationType" : NewSurfaceOperationType.NEW, "entities" : qUnion([Q0]), "axis" : qUnion([Q1]), "revolveType" : RevolveType.FULL});
        }
    });
